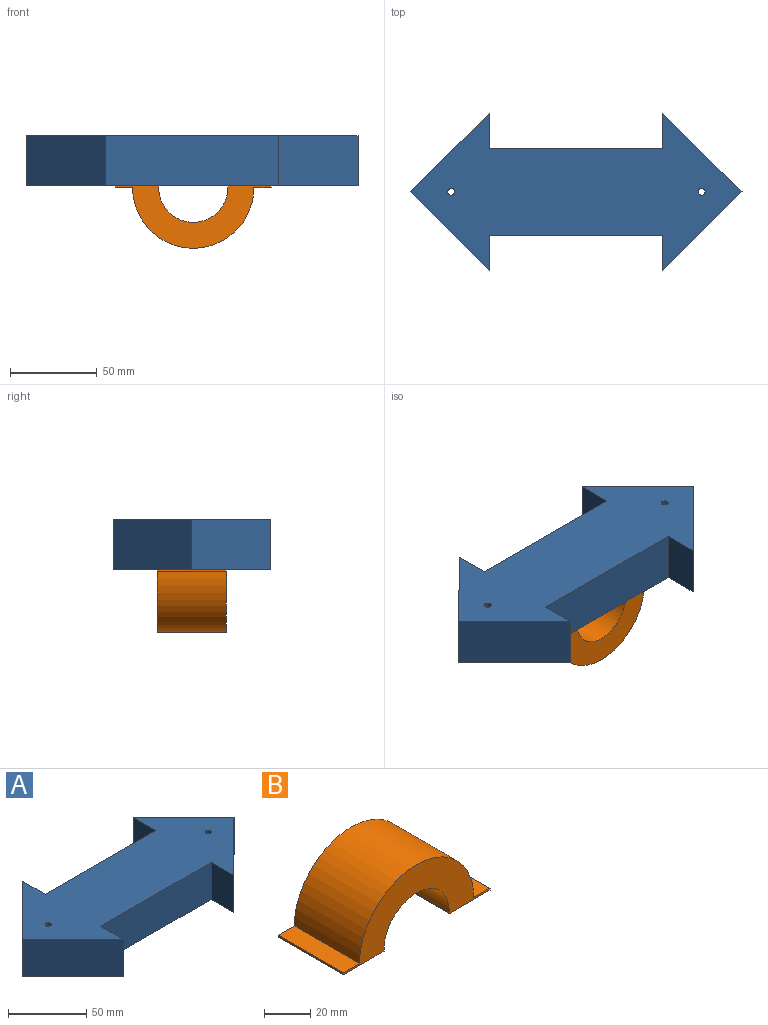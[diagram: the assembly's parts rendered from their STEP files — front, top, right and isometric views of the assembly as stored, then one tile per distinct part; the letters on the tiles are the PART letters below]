
ASSEMBLY  parts=2 mates=1
PART A: 27 faces, bbox 191.7x91.1x29 mm
  f0: plane 100x29mm, normal (0,-1,0), area 2900mm2, adj f5,f6,f10,f21
  f1: plane 100x29mm, normal (0,1,0), area 2900mm2, adj f2,f9,f10,f21
  f2: plane 29x20.44mm, normal (1,0,0), area 592.7mm2, adj f1,f3,f10,f21
  f3: plane 46.06x45.44mm, normal (-0.7,0.71,0), area 1876.4mm2, adj f2,f4,f10,f21
  f4: plane 46.06x45.62mm, normal (-0.7,-0.71,0), area 1880mm2, adj f3,f5,f10,f21
  f5: plane 29x20.62mm, normal (1,0,0), area 597.9mm2, adj f0,f4,f10,f21
  f6: plane 29x20.41mm, normal (-1,0,0), area 591.9mm2, adj f0,f7,f10,f21
  f7: plane 45.64x45.41mm, normal (0.71,-0.71,0), area 1867.1mm2, adj f6,f8,f10,f21
  f8: plane 45.64x45.16mm, normal (0.7,0.71,0), area 1861.9mm2, adj f7,f9,f10,f21
  f9: plane 29x20.16mm, normal (-1,0,0), area 584.5mm2, adj f1,f8,f10,f21
  f10: plane 191.7x91.06mm, normal (0,0,1), area 9138.7mm2, adj f0,f1,f2,f3,f4,f5,f6,f7
  f11: plane 80.2x27mm, normal (-1,0,0), area 1030.3mm2, adj f12,f13,f14,f19,f20,f21,f22
  f12: plane 40.57x40.02mm, normal (0.7,-0.71,0), area 1538.6mm2, adj f11,f13,f20,f21
  f13: plane 40.57x40.18mm, normal (0.7,0.71,0), area 1541.7mm2, adj f11,f12,f20,f21
  f14: plane 100.6x25mm, normal (0,1,0), area 2514.9mm2, adj f11,f15,f20,f22
  f15: plane 25x2mm, normal (0,1,0), area 50mm2, adj f14,f16,f20,f22
  f16: plane 79.69x27mm, normal (1,0,0), area 1019.2mm2, adj f15,f17,f18,f19,f20,f21,f22
  f17: plane 40.16x39.96mm, normal (-0.71,0.71,0), area 1529.6mm2, adj f16,f18,f20,f21
  f18: plane 40.16x39.73mm, normal (-0.7,-0.71,0), area 1525.2mm2, adj f16,f17,f20,f21
  f19: plane 102.6x25mm, normal (0,-1,0), area 2564.9mm2, adj f11,f16,f20,f22
  f20: plane 183.32x80.2mm, normal (0,0,-1), area 7854.6mm2, adj f11,f12,f13,f14,f15,f16,f17,f18
  f21: plane 191.7x91.06mm, normal (0,0,-1), area 5930.7mm2, adj f0,f1,f2,f3,f4,f5,f6,f7
  f22: plane 102.6x45.41mm, normal (0,0,1), area 4646.6mm2, adj f11,f14,f15,f16,f19,f25,f26
  f23: cylinder r=2mm len=4mm, axis (0,0,1), area 25.1mm2, adj f10,f20
  f24: cylinder r=2mm len=4mm, axis (0,0,1), area 25.1mm2, adj f10,f20
  f25: cylinder r=1mm len=2mm, axis (0,0,-1), area 12.6mm2, adj f21,f22
  f26: cylinder r=1mm len=2mm, axis (0,0,-1), area 12.6mm2, adj f21,f22
PART B: 16 faces, bbox 90x40x36 mm
  f0: cylinder r=35mm len=70mm, axis (0,-1,0), area 4398.2mm2, adj f1,f3,f6,f10
  f1: plane 90x36mm, normal (0,-1,0), area 1345.9mm2, adj f0,f2,f4,f5,f6,f7,f8,f9
  f2: cylinder r=20mm len=40mm, axis (0,-1,0), area 2513.3mm2, adj f1,f3,f4,f8
  f3: plane 90x36mm, normal (0,1,0), area 1345.9mm2, adj f0,f2,f4,f5,f6,f7,f8,f9
  f4: plane 40x1mm, normal (-1,0,0), area 40mm2, adj f1,f2,f3,f5
  f5: plane 40x25mm, normal (0,0,-1), area 996.9mm2, adj f1,f3,f4,f7,f15
  f6: plane 40x10mm, normal (0,0,1), area 400mm2, adj f0,f1,f3,f7
  f7: plane 40x1mm, normal (1,0,0), area 40mm2, adj f1,f3,f5,f6
  f8: plane 40x1mm, normal (1,0,0), area 40mm2, adj f1,f2,f3,f9
  f9: plane 40x25mm, normal (0,0,-1), area 996.9mm2, adj f1,f3,f8,f11,f13
  f10: plane 40x10mm, normal (0,0,1), area 400mm2, adj f0,f1,f3,f11
  f11: plane 40x1mm, normal (-1,0,0), area 40mm2, adj f1,f3,f9,f10
  f12: cone r=0mm half-angle=59deg, axis (0,0,-1), area 3.7mm2, adj f13
  f13: cylinder r=1mm len=2mm, axis (0,0,-1), area 12.6mm2, adj f9,f12
  f14: cone r=0mm half-angle=59deg, axis (0,0,-1), area 3.7mm2, adj f15
  f15: cylinder r=1mm len=2mm, axis (0,0,-1), area 12.6mm2, adj f5,f14
PLACE A t=(-26.19,-30.11,4.98)mm
PLACE B rot(axis=(1,0,0),180deg) t=(-17.04,-1,-23.02)mm
MATE fastened B.f12 <-> A.f26  axis (0,0,1) through (-50.04,-30.65,-22.02)mm
